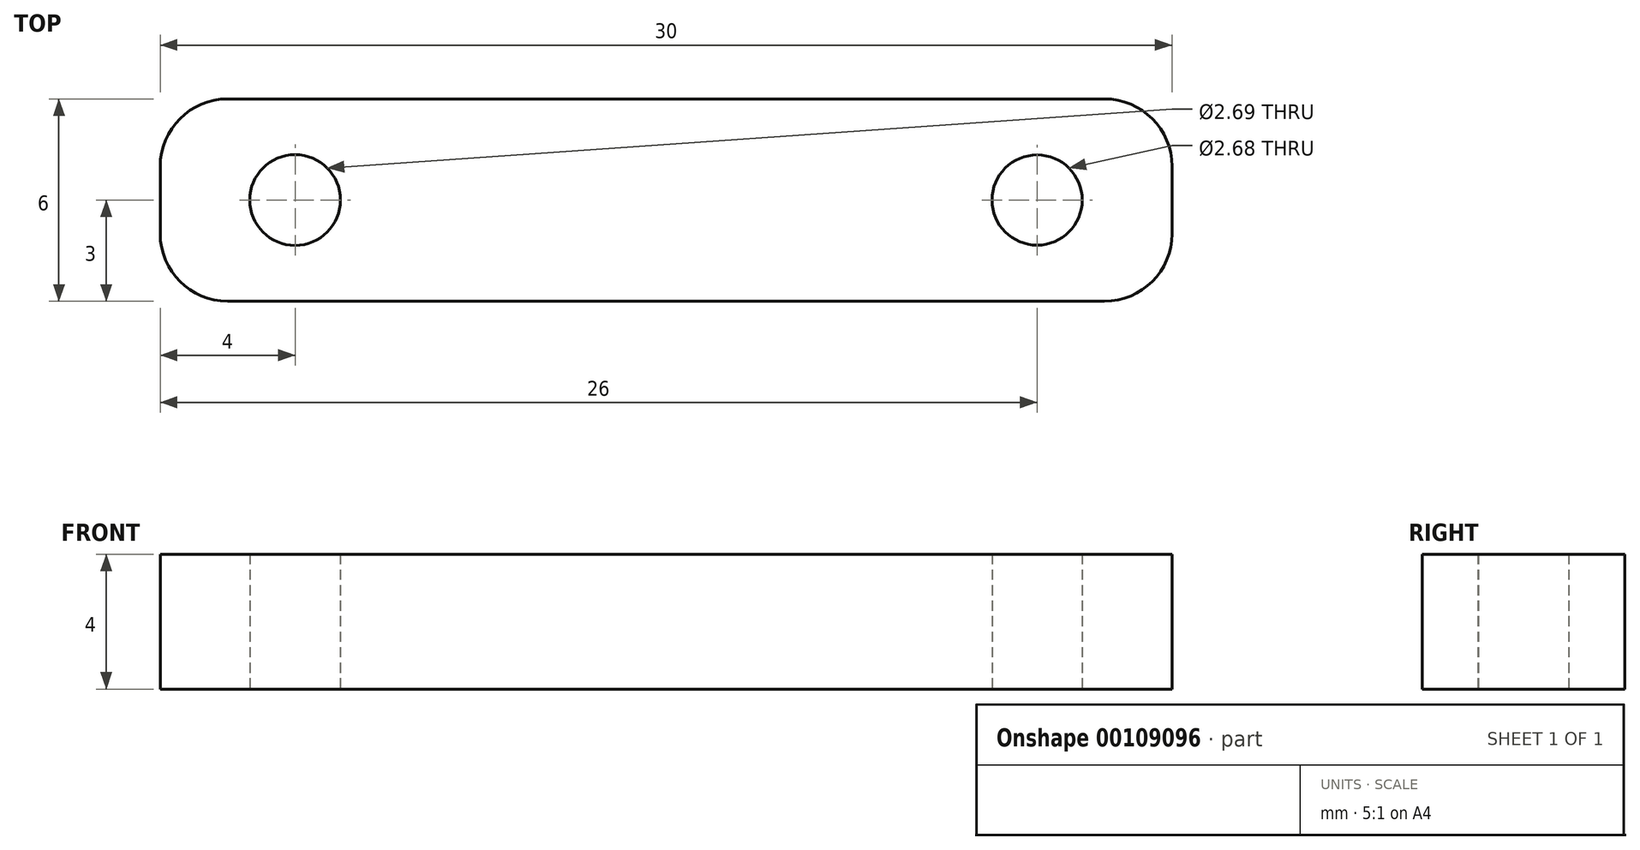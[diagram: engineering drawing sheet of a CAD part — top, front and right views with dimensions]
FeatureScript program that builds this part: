
annotation { "Feature Type Name" : "Feature", "Feature Type Description" : "" }
export const myFeature = defineFeature(function(context is Context, id is Id, definition is map)
    precondition{}
    {
        {
            var Q0;
            Q0=qCreatedBy(makeId("Top.planeOp"),FACE);
            var sketch = newSketch(context, id + "F0", { "sketchPlane" : qUnion([Q0])});
            skLineSegment(sketch, "E0.bottom", {"start": v(13, 3) * mm, "end": v(-13, 3) * mm});
            skLineSegment(sketch, "E0.top", {"start": v(13, -3) * mm, "end": v(-13, -3) * mm});
            skLineSegment(sketch, "E0.left", {"start": v(15, 1) * mm, "end": v(15, -1) * mm});
            skLineSegment(sketch, "E0.right", {"start": v(-15, 1) * mm, "end": v(-15, -1) * mm});
            skPoint(sketch, "E0.middle", {"position": v(0, 0) * mm});
            skCircle(sketch, "E1", {"center": v(-11, 0) * mm, "radius": 1.34 * mm});
            skCircle(sketch, "E2", {"center": v(11, 0) * mm, "radius": 1.34 * mm});
            skPoint(sketch, "E3.visualSharp", {"position": v(-15, 3) * mm});
            skArc(sketch, "E3.filletArc", {"start": v(-13, 3) * mm, "mid": v(-14.41, 2.41) * mm, "end": v(-15, 1) * mm});
            skPoint(sketch, "E4.visualSharp", {"position": v(-15, -3) * mm});
            skArc(sketch, "E4.filletArc", {"start": v(-15, -1) * mm, "mid": v(-14.41, -2.41) * mm, "end": v(-13, -3) * mm});
            skPoint(sketch, "E5.visualSharp", {"position": v(15, 3) * mm});
            skArc(sketch, "E5.filletArc", {"start": v(15, 1) * mm, "mid": v(14.41, 2.41) * mm, "end": v(13, 3) * mm});
            skPoint(sketch, "E6.visualSharp", {"position": v(15, -3) * mm});
            skArc(sketch, "E6.filletArc", {"start": v(13, -3) * mm, "mid": v(14.41, -2.41) * mm, "end": v(15, -1) * mm});
            skSolve(sketch);
        }
        {
            var Q0;
            Q0=makeQuery(id+"F0.imprint","IMPRINT",FACE,{"disambiguationData":[TD([[makeQuery(id+"F0.imprint","IMPRINT",EDGE,{"derivedFrom":sQuery(id+"F0.wireOp",EDGE,"E0.bottom")}),1.0]])]});
            extrude(context, id + "F1", {"entities" : qUnion([Q0]), "depth" : 4 * mm});
        }
    });
